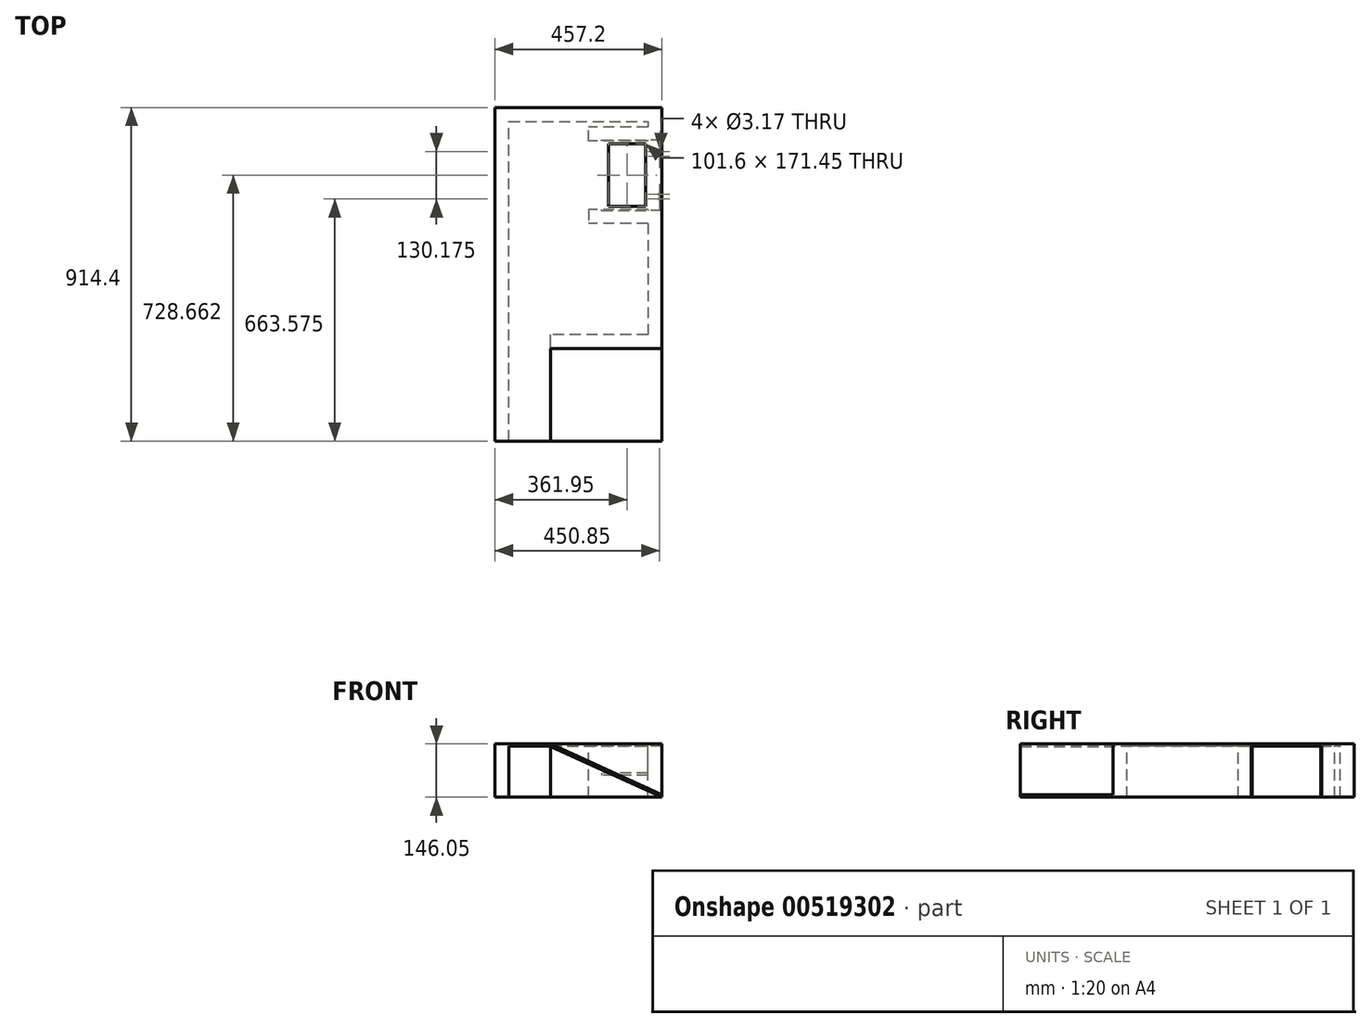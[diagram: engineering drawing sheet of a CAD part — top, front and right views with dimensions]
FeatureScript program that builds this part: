
annotation { "Feature Type Name" : "Feature", "Feature Type Description" : "" }
export const myFeature = defineFeature(function(context is Context, id is Id, definition is map)
    precondition{}
    {
        {
            var Q0;
            Q0=qCreatedBy(makeId("Top.planeOp"),FACE);
            var sketch = newSketch(context, id + "F0", { "sketchPlane" : qUnion([Q0])});
            skLineSegment(sketch, "E0.0", {"start": v(-228.6, 457.2) * mm, "end": v(228.6, 457.2) * mm});
            skLineSegment(sketch, "E0.1", {"start": v(228.6, 457.2) * mm, "end": v(228.6, -457.2) * mm});
            skLineSegment(sketch, "E0.2", {"start": v(228.6, -457.2) * mm, "end": v(-228.6, -457.2) * mm});
            skLineSegment(sketch, "E0.3", {"start": v(-228.6, -457.2) * mm, "end": v(-228.6, 457.2) * mm});
            skPoint(sketch, "E0.0.midPoint", {"position": v(0, 457.2) * mm});
            skPoint(sketch, "E0.cCircle.center.orphan", {"position": v(0, 0) * mm});
            skLineSegment(sketch, "E1.bottom", {"start": v(184.15, 357.19) * mm, "end": v(82.55, 357.19) * mm});
            skLineSegment(sketch, "E1.top", {"start": v(184.15, 185.74) * mm, "end": v(82.55, 185.74) * mm});
            skLineSegment(sketch, "E1.left", {"start": v(184.15, 357.19) * mm, "end": v(184.15, 185.74) * mm});
            skLineSegment(sketch, "E1.right", {"start": v(82.55, 357.19) * mm, "end": v(82.55, 185.74) * mm});
            skSolve(sketch);
        }
        {
            var Q0;
            Q0=makeQuery(id+"F0.imprint","IMPRINT",FACE,{"disambiguationData":[TD([[makeQuery(id+"F0.imprint","IMPRINT",EDGE,{"derivedFrom":sQuery(id+"F0.wireOp",EDGE,"E0.0")}),-1.0]])]});
            extrude(context, id + "F1", {"entities" : qUnion([Q0]), "depth" : 6.35 * mm, "offsetDistance" : 25.4 * mm});
        }
        {
            var Q0;
            Q0=makeQuery(id+"F1.opExtrude","CAP_FACE",FACE,{"disambiguationData":[OSD([sQuery(id+"F0.wireOp",EDGE,"E0.0"),sQuery(id+"F0.wireOp",EDGE,"E0.1"),sQuery(id+"F0.wireOp",EDGE,"E0.2"),sQuery(id+"F0.wireOp",EDGE,"E0.3"),sQuery(id+"F0.wireOp",EDGE,"E1.bottom"),sQuery(id+"F0.wireOp",EDGE,"E1.top"),sQuery(id+"F0.wireOp",EDGE,"E1.left"),sQuery(id+"F0.wireOp",EDGE,"E1.right")])],"isStart":true});
            var sketch = newSketch(context, id + "F2", { "sketchPlane" : qUnion([Q0])});
            skLineSegment(sketch, "E2.bottom", {"start": v(-228.6, 457.2) * mm, "end": v(-190.5, 457.2) * mm});
            skLineSegment(sketch, "E2.top", {"start": v(-228.6, -457.2) * mm, "end": v(-190.5, -457.2) * mm});
            skLineSegment(sketch, "E2.left", {"start": v(-228.6, 457.2) * mm, "end": v(-228.6, -457.2) * mm});
            skLineSegment(sketch, "E2.right", {"start": v(-190.5, 457.2) * mm, "end": v(-190.5, -457.2) * mm});
            skLineSegment(sketch, "E3.bottom", {"start": v(-190.5, -419.1) * mm, "end": v(190.5, -419.1) * mm});
            skLineSegment(sketch, "E3.top", {"start": v(-190.5, -457.2) * mm, "end": v(190.5, -457.2) * mm});
            skLineSegment(sketch, "E3.left", {"start": v(-190.5, -419.1) * mm, "end": v(-190.5, -457.2) * mm});
            skLineSegment(sketch, "E3.right", {"start": v(190.5, -419.1) * mm, "end": v(190.5, -457.2) * mm});
            skLineSegment(sketch, "E4.bottom", {"start": v(228.6, -457.2) * mm, "end": v(190.5, -457.2) * mm});
            skLineSegment(sketch, "E4.top", {"start": v(228.6, -368.3) * mm, "end": v(190.5, -368.3) * mm});
            skLineSegment(sketch, "E4.left", {"start": v(228.6, -457.2) * mm, "end": v(228.6, -368.3) * mm});
            skLineSegment(sketch, "E4.right", {"start": v(190.5, -457.2) * mm, "end": v(190.5, -368.3) * mm});
            skLineSegment(sketch, "E5.bottom", {"start": v(228.6, -174.63) * mm, "end": v(190.5, -174.63) * mm});
            skLineSegment(sketch, "E5.top", {"start": v(228.6, 203.2) * mm, "end": v(190.5, 203.2) * mm});
            skLineSegment(sketch, "E5.left", {"start": v(228.6, -174.63) * mm, "end": v(228.6, 203.2) * mm});
            skLineSegment(sketch, "E5.right", {"start": v(190.5, -174.63) * mm, "end": v(190.5, 203.2) * mm});
            skLineSegment(sketch, "E6.bottom", {"start": v(190.5, 203.2) * mm, "end": v(-76.2, 203.2) * mm});
            skLineSegment(sketch, "E6.top", {"start": v(190.5, 165.1) * mm, "end": v(-76.2, 165.1) * mm});
            skLineSegment(sketch, "E6.left", {"start": v(190.5, 203.2) * mm, "end": v(190.5, 165.1) * mm});
            skLineSegment(sketch, "E6.right", {"start": v(-76.2, 203.2) * mm, "end": v(-76.2, 165.1) * mm});
            skLineSegment(sketch, "E7.bottom", {"start": v(190.5, -365.13) * mm, "end": v(28.58, -365.13) * mm});
            skLineSegment(sketch, "E7.top", {"start": v(190.5, -403.23) * mm, "end": v(28.58, -403.23) * mm});
            skLineSegment(sketch, "E7.left", {"start": v(190.5, -365.13) * mm, "end": v(190.5, -403.23) * mm});
            skLineSegment(sketch, "E7.right", {"start": v(28.58, -365.13) * mm, "end": v(28.58, -403.23) * mm});
            skLineSegment(sketch, "E8.bottom", {"start": v(190.5, -177.8) * mm, "end": v(28.57, -177.8) * mm});
            skLineSegment(sketch, "E8.top", {"start": v(190.5, -139.7) * mm, "end": v(28.57, -139.7) * mm});
            skLineSegment(sketch, "E8.left", {"start": v(190.5, -177.8) * mm, "end": v(190.5, -139.7) * mm});
            skLineSegment(sketch, "E8.right", {"start": v(28.57, -177.8) * mm, "end": v(28.57, -139.7) * mm});
            skLineSegment(sketch, "E9.bottom", {"start": v(28.57, -177.8) * mm, "end": v(66.68, -177.8) * mm});
            skLineSegment(sketch, "E9.top", {"start": v(28.57, -365.13) * mm, "end": v(66.68, -365.13) * mm});
            skLineSegment(sketch, "E9.left", {"start": v(28.57, -177.8) * mm, "end": v(28.57, -365.13) * mm});
            skLineSegment(sketch, "E9.right", {"start": v(66.68, -177.8) * mm, "end": v(66.68, -365.13) * mm});
            skSolve(sketch);
        }
        {
            var Q0;
            Q0=makeQuery(id+"F2.imprint","IMPRINT",FACE,{"disambiguationData":[TD([[makeQuery(id+"F2.imprint","IMPRINT",EDGE,{"derivedFrom":sQuery(id+"F2.wireOp",EDGE,"E2.bottom")}),1.0]])]});
            var Q1;
            {var subQ0=sQuery(id+"F2.wireOp",EDGE,"E3.bottom");Q1=makeQuery(id+"F2.imprint","IMPRINT",FACE,{"disambiguationData":[TD([[makeQuery(id+"F2.imprint","IMPRINT",EDGE,{"derivedFrom":subQ0}),-1.0]])]});}
            var Q2;
            {var subQ2=sQuery(id+"F2.wireOp",EDGE,"E4.bottom");Q2=makeQuery(id+"F2.imprint","IMPRINT",FACE,{"disambiguationData":[TD([[makeQuery(id+"F2.imprint","IMPRINT",EDGE,{"derivedFrom":subQ2}),1.0]])]});}
            var Q3;
            Q3=makeQuery(id+"F2.imprint","IMPRINT",FACE,{"disambiguationData":[TD([[makeQuery(id+"F2.imprint","IMPRINT",EDGE,{"derivedFrom":sQuery(id+"F2.wireOp",EDGE,"E5.bottom")}),-1.0]])]});
            var Q4;
            Q4=makeQuery(id+"F2.imprint","IMPRINT",FACE,{"disambiguationData":[TD([[makeQuery(id+"F2.imprint","IMPRINT",EDGE,{"derivedFrom":sQuery(id+"F2.wireOp",EDGE,"E6.bottom")}),1.0]])]});
            var Q5;
            {var subQ3=sQuery(id+"F2.wireOp",EDGE,"E7.bottom");Q5=makeQuery(id+"F2.imprint","IMPRINT",FACE,{"disambiguationData":[TD([[makeQuery(id+"F2.imprint","IMPRINT",EDGE,{"derivedFrom":subQ3}),1.0]])]});}
            var Q6;
            Q6=makeQuery(id+"F2.imprint","IMPRINT",FACE,{"disambiguationData":[TD([[makeQuery(id+"F2.imprint","IMPRINT",EDGE,{"derivedFrom":sQuery(id+"F2.wireOp",EDGE,"E9.bottom")}),-1.0]])]});
            var Q7;
            {var subQ3=sQuery(id+"F2.wireOp",EDGE,"E8.bottom");Q7=makeQuery(id+"F2.imprint","IMPRINT",FACE,{"disambiguationData":[TD([[makeQuery(id+"F2.imprint","IMPRINT",EDGE,{"derivedFrom":subQ3}),-1.0]])]});}
            extrude(context, id + "F3", {"entities" : qUnion([Q0, Q1, Q2, Q3, Q4, Q5, Q6, Q7]), "operationType" : NewBodyOperationType.ADD, "depth" : 139.7 * mm, "offsetDistance" : 25.4 * mm});
        }
        {
            var Q0;
            Q0=makeQuery(id+"F3.boolean.opBoolean","MERGE",FACE,{"derivedFrom":[makeQuery(id+"F1.opExtrude","SWEPT_FACE",FACE,{"disambiguationData":[OSD([sQuery(id+"F0.wireOp",EDGE,"E0.1")])]}),makeQuery(id+"F3.opExtrude","SWEPT_FACE",FACE,{"disambiguationData":[OSD([sQuery(id+"F2.wireOp",EDGE,"E4.left")])]}),makeQuery(id+"F3.opExtrude","SWEPT_FACE",FACE,{"disambiguationData":[OSD([sQuery(id+"F2.wireOp",EDGE,"E5.left")])]})]});
            var sketch = newSketch(context, id + "F4", { "sketchPlane" : qUnion([Q0])});
            skLineSegment(sketch, "E10.bottom", {"start": v(174.63, -73.03) * mm, "end": v(368.3, -73.03) * mm});
            skLineSegment(sketch, "E10.top", {"start": v(174.63, -79.38) * mm, "end": v(368.3, -79.38) * mm});
            skLineSegment(sketch, "E10.left", {"start": v(174.63, -73.03) * mm, "end": v(174.63, -79.38) * mm});
            skLineSegment(sketch, "E10.right", {"start": v(368.3, -73.03) * mm, "end": v(368.3, -79.38) * mm});
            skSolve(sketch);
        }
        {
            var Q0;
            Q0=makeQuery(id+"F4.imprint","IMPRINT",FACE,{"disambiguationData":[TD([[makeQuery(id+"F4.imprint","IMPRINT",EDGE,{"derivedFrom":sQuery(id+"F4.wireOp",EDGE,"E10.bottom")}),-1.0]])]});
            extrude(context, id + "F5", {"entities" : qUnion([Q0]), "operationType" : NewBodyOperationType.REMOVE, "oppositeDirection" : true, "depth" : 165.1 * mm, "offsetDistance" : 25.4 * mm});
        }
        {
            var Q0;
            Q0=makeQuery(id+"F1.opExtrude","CAP_FACE",FACE,{"disambiguationData":[OSD([sQuery(id+"F0.wireOp",EDGE,"E0.0"),sQuery(id+"F0.wireOp",EDGE,"E0.1"),sQuery(id+"F0.wireOp",EDGE,"E0.2"),sQuery(id+"F0.wireOp",EDGE,"E0.3"),sQuery(id+"F0.wireOp",EDGE,"E1.bottom"),sQuery(id+"F0.wireOp",EDGE,"E1.top"),sQuery(id+"F0.wireOp",EDGE,"E1.left"),sQuery(id+"F0.wireOp",EDGE,"E1.right")])],"isStart":false});
            var sketch = newSketch(context, id + "F6", { "sketchPlane" : qUnion([Q0])});
            skLineSegment(sketch, "E11.bottom", {"start": v(228.6, -457.2) * mm, "end": v(-76.2, -457.2) * mm});
            skLineSegment(sketch, "E11.top", {"start": v(228.6, -203.2) * mm, "end": v(-76.2, -203.2) * mm});
            skLineSegment(sketch, "E11.left", {"start": v(228.6, -457.2) * mm, "end": v(228.6, -203.2) * mm});
            skLineSegment(sketch, "E11.right", {"start": v(-76.2, -457.2) * mm, "end": v(-76.2, -203.2) * mm});
            skSolve(sketch);
        }
        {
            var Q0;
            Q0=makeQuery(id+"F6.imprint","IMPRINT",FACE,{"disambiguationData":[TD([[makeQuery(id+"F6.imprint","IMPRINT",EDGE,{"derivedFrom":sQuery(id+"F6.wireOp",EDGE,"E11.bottom")}),-1.0]])]});
            extrude(context, id + "F7", {"entities" : qUnion([Q0]), "operationType" : NewBodyOperationType.REMOVE, "oppositeDirection" : true, "depth" : 12.7 * mm, "offsetDistance" : 25.4 * mm});
        }
        {
            var Q0;
            Q0=makeQuery(id+"F7.boolean.opBoolean","MERGE",FACE,{"derivedFrom":[makeQuery(id+"F3.opExtrude","SWEPT_FACE",FACE,{"disambiguationData":[OSD([sQuery(id+"F2.wireOp",EDGE,"E5.top"),sQuery(id+"F2.wireOp",EDGE,"E6.bottom")])]}),makeQuery(id+"F7.opExtrude","SWEPT_FACE",FACE,{"disambiguationData":[OSD([sQuery(id+"F6.wireOp",EDGE,"E11.top")])]})]});
            var sketch = newSketch(context, id + "F8", { "sketchPlane" : qUnion([Q0])});
            skLineSegment(sketch, "E12", {"start": v(-76.2, 6.35) * mm, "end": v(231.24, -133.92) * mm, "construction": true});
            skLineSegment(sketch, "E13", {"start": v(228.6, -139.7) * mm, "end": v(-76.2, -0.63) * mm, "construction": true});
            skLineSegment(sketch, "E14", {"start": v(228.6, -139.7) * mm, "end": v(231.24, -133.92) * mm, "construction": true});
            skLineSegment(sketch, "E15", {"start": v(-76.2, 6.35) * mm, "end": v(-76.2, -0.63) * mm});
            skLineSegment(sketch, "E16", {"start": v(-76.2, -0.63) * mm, "end": v(228.6, -139.7) * mm});
            skLineSegment(sketch, "E17", {"start": v(228.6, -139.7) * mm, "end": v(231.24, -133.92) * mm});
            skLineSegment(sketch, "E18", {"start": v(231.24, -133.92) * mm, "end": v(-76.2, 6.35) * mm});
            skSolve(sketch);
        }
        {
            var Q0;
            {var subQ0=sQuery(id+"F8.wireOp",EDGE,"E16");Q0=makeQuery(id+"F8.imprint","IMPRINT",FACE,{"disambiguationData":[TD([[makeQuery(id+"F8.imprint","IMPRINT",EDGE,{"derivedFrom":subQ0}),1.0]])]});}
            extrude(context, id + "F9", {"entities" : qUnion([Q0]), "operationType" : NewBodyOperationType.ADD, "depth" : 254 * mm, "offsetDistance" : 25.4 * mm});
        }
        {
            var Q0;
            Q0=makeQuery(id+"F1.opExtrude","CAP_FACE",FACE,{"disambiguationData":[OSD([sQuery(id+"F0.wireOp",EDGE,"E0.0"),sQuery(id+"F0.wireOp",EDGE,"E0.1"),sQuery(id+"F0.wireOp",EDGE,"E0.2"),sQuery(id+"F0.wireOp",EDGE,"E0.3"),sQuery(id+"F0.wireOp",EDGE,"E1.bottom"),sQuery(id+"F0.wireOp",EDGE,"E1.top"),sQuery(id+"F0.wireOp",EDGE,"E1.left"),sQuery(id+"F0.wireOp",EDGE,"E1.right")])],"isStart":false});
            var sketch = newSketch(context, id + "F10", { "sketchPlane" : qUnion([Q0])});
            skLineSegment(sketch, "E19", {"start": v(222.25, 368.3) * mm, "end": v(222.25, 174.63) * mm, "construction": true});
            skPoint(sketch, "E20", {"position": v(222.25, 336.55) * mm});
            skPoint(sketch, "E21", {"position": v(222.25, 323.85) * mm});
            skPoint(sketch, "E22", {"position": v(222.25, 219.08) * mm});
            skPoint(sketch, "E23", {"position": v(222.25, 206.38) * mm});
            skSolve(sketch);
        }
        {
            var Q0;
            Q0=sQuery(id+"F10.wireOp",VERTEX,"E20");
            var Q1;
            Q1=sQuery(id+"F10.wireOp",VERTEX,"E21");
            var Q2;
            Q2=sQuery(id+"F10.wireOp",VERTEX,"E22");
            var Q3;
            Q3=sQuery(id+"F10.wireOp",VERTEX,"E23");
            var Q4;
            Q4=makeQuery(id+"F1.opExtrude","SWEPT_BODY",BODY,{"disambiguationData":[OSD([sQuery(id+"F0.wireOp",EDGE,"E0.0"),sQuery(id+"F0.wireOp",EDGE,"E0.1"),sQuery(id+"F0.wireOp",EDGE,"E0.2"),sQuery(id+"F0.wireOp",EDGE,"E0.3"),sQuery(id+"F0.wireOp",EDGE,"E1.bottom"),sQuery(id+"F0.wireOp",EDGE,"E1.top"),sQuery(id+"F0.wireOp",EDGE,"E1.left"),sQuery(id+"F0.wireOp",EDGE,"E1.right")])]});
            hole(context, id + "F11", {"style" : HoleStyle.SIMPLE, "endStyle" : HoleEndStyle.THROUGH, "holeDiameter" : 3.17 * mm, "isTappedThrough" : true, "tappedDepth" : 12.7 * mm, "tapClearance" : 3, "locations" : qUnion([Q0, Q1, Q2, Q3]), "scope" : qUnion([Q4])});
        }
    });
